FCSTD DOCUMENT  (FreeCAD 1.0R39319 (Git))
Label: K93-10436-H7-L120_reference_4mmBanana_slot1_up
License: All rights reserved
LicenseURL: https://en.wikipedia.org/wiki/All_rights_reserved
objects: App::FeaturePython×5, App::Link×3, Assembly::JointGroup×1, Assembly::AssemblyObject×1
EXTERNAL_REF file=K93-10436-H7-L120.FCStd obj=K93_120
EXTERNAL_REF file=K93-10436-H7-L120_frontpanel_4mmBanana_slot1_up.FCStd obj=Body
EXTERNAL_REF file=Reference_4mmBanana.FCStd obj=Reference_banana4mm_1

FEATURE [App::Link] K93_120  label="K93-120"
  LinkPlacement = pos=(0,127.688,112.312) rot=(1,0,0;1.5708rad)
  LinkedObject = -> <external K93-10436-H7-L120.FCStd>#K93_120
  Placement = pos=(0,127.688,112.312) rot=(1,0,0;1.5708rad)
FEATURE [App::FeaturePython] GroundedJoint  # Assembly grounded joint (typed FeaturePython)
  ObjectToGround = -> K93_120
  Placement = pos=(0,127.688,112.312) rot=(1,0,0;1.5708rad)
FEATURE [App::Link] Body  label="K93-10436-H7-L120_frontpanel_4mmBanana_slot1_up"
  LinkPlacement = pos=(2.87919,-53.0619,120.006) rot=(1,0,0;1.5708rad)
  LinkedObject = -> <external K93-10436-H7-L120_frontpanel_4mmBanana_slot1_up.FCStd>#Body
  Placement = pos=(2.87919,-53.0619,120.006) rot=(1,0,0;1.5708rad)
FEATURE [App::FeaturePython] Joint  label="Fixed"  # Assembly joint (typed FeaturePython)
  Activated = true
  AngleMax = 0
  AngleMin = 0
  Detach1 = false
  Detach2 = false
  Distance = 0
  Distance2 = 0
  EnableAngleMax = false
  EnableAngleMin = false
  EnableLengthMax = false
  EnableLengthMin = false
  JointType = 0 (Fixed)
  LengthMax = 0
  LengthMin = 0
  Offset2 = pos=(0,0,0) rot=(0,0,1;3.14159rad)
  Placement1 = pos=(9.8e-15,0,60) rot=(0.707107,0,0.707107;3.14159rad)
  Placement2 = pos=(1.5024e-12,17.9943,-0.75) rot=(0,1,0;4.71239rad)
  Reference1 = -> Assembly [K93_120.Part__Feature001.Edge190,K93_120.Part__Feature001.Edge190]
  Reference2 = -> Assembly [Body.Edge37,Body.Edge37]
FEATURE [App::Link] Reference_banana4mm_1  label="Reference_banana4mm 1"
  LinkPlacement = pos=(2.87919,7.68808,111.34) rot=(0.99808,0,0;0rad)
  LinkedObject = -> <external Reference_4mmBanana.FCStd>#Reference_banana4mm_1
  Placement = pos=(2.87919,7.68808,111.34) rot=(0.99808,0,0;0rad)
FEATURE [App::FeaturePython] Joint001  label="Distance"  # Assembly joint (typed FeaturePython)
  Activated = true
  AngleMax = 0
  AngleMin = 0
  Detach1 = false
  Detach2 = false
  Distance = -0.2
  Distance2 = 0
  EnableAngleMax = false
  EnableAngleMin = false
  EnableLengthMax = false
  EnableLengthMin = false
  JointType = 5 (Distance)
  LengthMax = 0
  LengthMin = 0
  Offset1 = pos=(0,0,0) rot=(0,0,1;3.14159rad)
  Placement1 = pos=(-50,10.1,0) rot=(-0.707107,0,0.707107;3.14159rad)
  Placement2 = pos=(-49.8,1.8e-15,0.755) rot=(-0.57735,-0.57735,0.57735;2.0944rad)
  Reference1 = -> Assembly [K93_120.Part__Feature.Face87,K93_120.Part__Feature.Vertex116]
  Reference2 = -> Assembly [Reference_banana4mm_1.Part__Feature048.Face3,Reference_banana4mm_1.Part__Feature048.Vertex3]
FEATURE [App::FeaturePython] Joint002  label="Distance001"  # Assembly joint (typed FeaturePython)
  Activated = true
  AngleMax = 0
  AngleMin = 0
  Detach1 = false
  Detach2 = false
  Distance = 0.2
  Distance2 = 0
  EnableAngleMax = false
  EnableAngleMin = false
  EnableLengthMax = false
  EnableLengthMin = false
  JointType = 5 (Distance)
  LengthMax = 0
  LengthMin = 0
  Placement1 = pos=(4e-16,-59.8,0.755) rot=(0,-0.707107,0.707107;3.14159rad)
  Placement2 = pos=(1.58751,4.42551,60) rot=(0,0,1;0rad)
  Reference1 = -> Assembly [Reference_banana4mm_1.Part__Feature048.Face1,Reference_banana4mm_1.Part__Feature048.Vertex3]
  Reference2 = -> Assembly [K93_120.Part__Feature.Face58,K93_120.Part__Feature.Vertex116]
FEATURE [App::FeaturePython] Joint003  label="Distance002"  # Assembly joint (typed FeaturePython)
  Activated = true
  AngleMax = 0
  AngleMin = 0
  Detach1 = false
  Detach2 = false
  Distance = 0.25
  Distance2 = 0
  EnableAngleMax = false
  EnableAngleMin = false
  EnableLengthMax = false
  EnableLengthMin = false
  JointType = 5 (Distance)
  LengthMax = 0
  LengthMin = 0
  Placement1 = pos=(-48.85,11.1,0) rot=(-0.57735,-0.57735,0.57735;4.18879rad)
  Placement2 = pos=(8e-16,0.0390875,1.51) rot=(0,0,1;0rad)
  Reference1 = -> Assembly [K93_120.Part__Feature.Face78,K93_120.Part__Feature.Vertex159]
  Reference2 = -> Assembly [Reference_banana4mm_1.Part__Feature048.Face5,Reference_banana4mm_1.Part__Feature048.Vertex3]
FEATURE [Assembly::JointGroup] Joints
  Group = -> [GroundedJoint,Joint,Joint001,Joint002,Joint003]
FEATURE [Assembly::AssemblyObject] Assembly
  Group = -> [Joints,K93_120,GroundedJoint,Body,Joint,Reference_banana4mm_1,Joint001,Joint002,Joint003]
  Origin = -> Origin
  Type = Assembly

RESOLVED EXTERNAL PARTS (link-assembly join: the EXTERNAL_REF files above that resolve inside this repo's crawl, each included once):
---- part K93-10436-H7-L120_frontpanel_4mmBanana_slot1_up.FCStd = doc fcstd_d72c00be4d09 ----
FCSTD DOCUMENT  (FreeCAD 1.0R39319 (Git))
Label: K93-10436-H7-L120_frontpanel_4mmBanana_slot1_up
License: All rights reserved
LicenseURL: https://en.wikipedia.org/wiki/All_rights_reserved
objects: Part::Feature×1, PartDesign::FeatureBase×1, Sketcher::SketchObject×1, PartDesign::Pocket×1, PartDesign::LinearPattern×1, PartDesign::Body×1
note: 11 computed .brp shape members not serialized (recipe doc carries the construction recipe); baked Part::Feature solids carry a one-line shape summary decoded from their .brp

FEATURE [Part::Feature] Part__Feature  label="K93-B"
  shape: bbox 104 x 35.99 x 1.5 mm, 34 faces (baked)
FEATURE [PartDesign::FeatureBase] BaseFeature
  BaseFeature = -> Part__Feature
  Suppressed = false
FEATURE [Sketcher::SketchObject] Sketch
  ArcFitTolerance = 1e-06
  AttachmentSupport = -> [BaseFeature]
  ExternalGeometry = -> [BaseFeature]
  FullyConstrained = true
  MakeInternals = false
  MapMode = 5
  Placement = pos=(0,0,0.75) rot=(0,0,1;0rad)
  sketch-geometry (1):
    g0: Circle CenterX=-39.37 CenterY=1.92573 CenterZ=0 NormalX=0 NormalY=0 NormalZ=1 AngleXU=0 Radius=5.75
  constraints (3):
    c: Diameter(g0) = 11.5
    c: Distance(g0,g-3) = 12.63
    c: Distance(g0,g-4) = 19.92
FEATURE [PartDesign::Pocket] Pocket
  BaseFeature = -> BaseFeature
  Direction = (0,0,-1)
  Length = 5
  Length2 = 5
  Profile = -> Sketch
  ReferenceAxis = -> Sketch [N_Axis]
  Refine = true
  Suppressed = false
  Type = 0
FEATURE [PartDesign::LinearPattern] LinearPattern
  BaseFeature = -> Pocket
  Direction = -> Sketch [H_Axis]
  Length = 78.74
  Mode = 0
  Occurrences = 2
  Offset = 78.74
  Originals = -> [Pocket]
  Refine = true
  Suppressed = false
  TransformMode = 0
FEATURE [PartDesign::Body] Body
  AllowCompound = false
  BaseFeature = -> Part__Feature
  Group = -> [BaseFeature,Sketch,Pocket,LinearPattern]
  Origin = -> Origin
  Tip = -> LinearPattern
